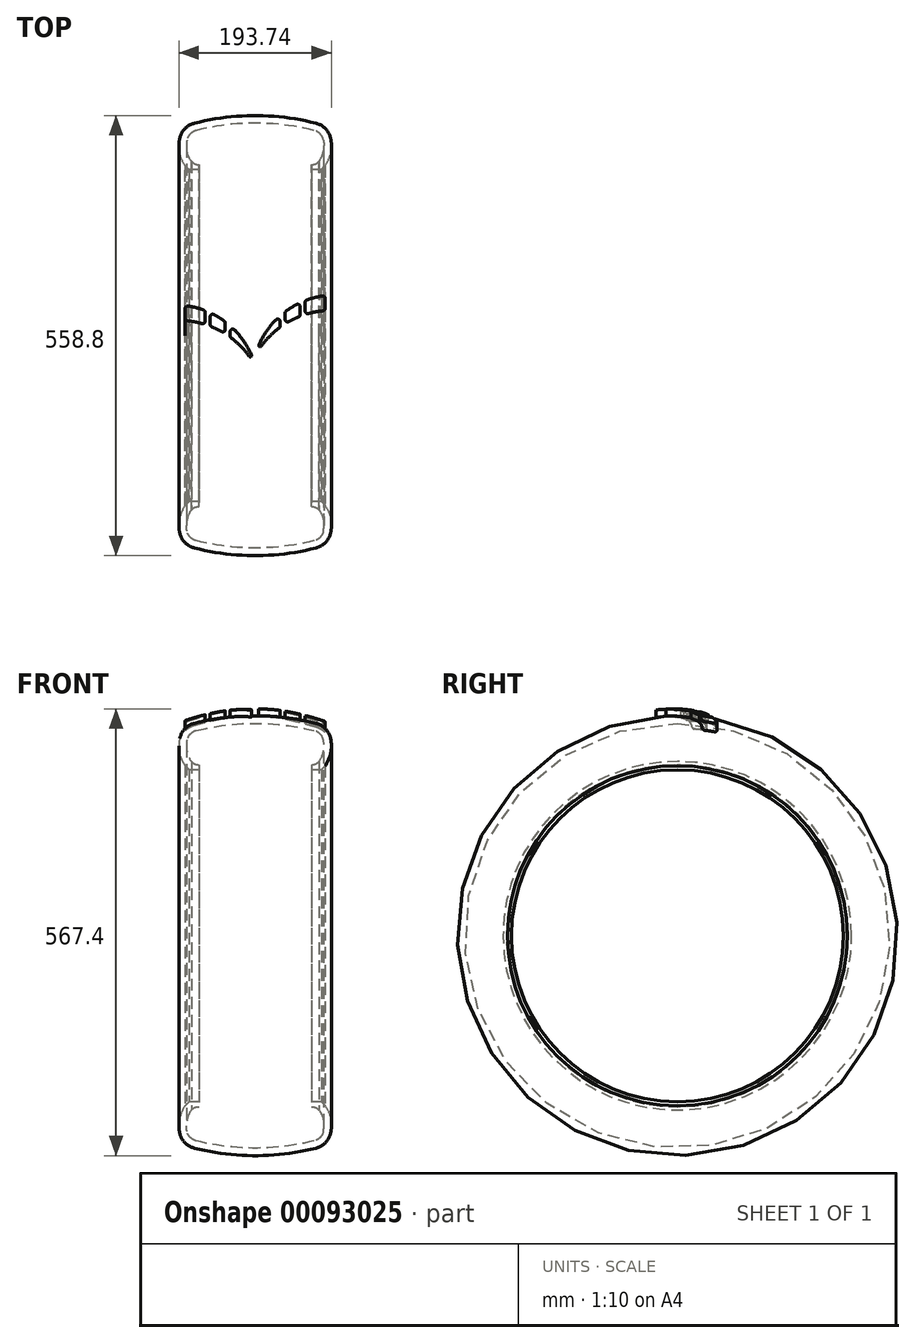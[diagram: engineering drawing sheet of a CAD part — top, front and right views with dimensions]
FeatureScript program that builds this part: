
annotation { "Feature Type Name" : "Feature", "Feature Type Description" : "" }
export const myFeature = defineFeature(function(context is Context, id is Id, definition is map)
    precondition{}
    {
        {
            var Q0;
            Q0=qCreatedBy(makeId("Front.planeOp"),FACE);
            var sketch = newSketch(context, id + "F0", { "sketchPlane" : qUnion([Q0])});
            skLineSegment(sketch, "E0", {"start": v(0, 0) * mm, "end": v(0, -279.4) * mm, "construction": true});
            skLineSegment(sketch, "E1", {"start": v(71.37, -210.82) * mm, "end": v(84.07, -210.82) * mm});
            skLineSegment(sketch, "E2", {"start": v(84.07, -210.82) * mm, "end": v(88.9, -215.9) * mm});
            skLineSegment(sketch, "E3.MirrorCS", {"start": v(-71.37, -210.82) * mm, "end": v(-84.07, -210.82) * mm});
            skLineSegment(sketch, "E4.MirrorCS", {"start": v(-84.07, -210.82) * mm, "end": v(-88.9, -215.9) * mm});
            skArc(sketch, "E5", {"start": v(95.92, -250.46) * mm, "mid": v(95.98, -232.45) * mm, "end": v(88.9, -215.9) * mm});
            skArc(sketch, "E6", {"start": v(0, -279.4) * mm, "mid": v(38.91, -277) * mm, "end": v(77.24, -269.86) * mm});
            skPoint(sketch, "E7.visualSharp", {"position": v(88.9, -266.7) * mm});
            skArc(sketch, "E7.filletArc", {"start": v(77.24, -269.86) * mm, "mid": v(89.36, -262.84) * mm, "end": v(95.92, -250.46) * mm});
            skArc(sketch, "E8.MirrorCS", {"start": v(0, -279.4) * mm, "mid": v(-38.91, -277) * mm, "end": v(-77.24, -269.86) * mm});
            skArc(sketch, "E9.MirrorCS", {"start": v(-77.24, -269.86) * mm, "mid": v(-89.36, -262.84) * mm, "end": v(-95.92, -250.46) * mm});
            skArc(sketch, "E10.MirrorCS", {"start": v(-95.92, -250.46) * mm, "mid": v(-95.98, -232.45) * mm, "end": v(-88.9, -215.9) * mm});
            skLineSegment(sketch, "E11", {"start": v(71.37, -210.82) * mm, "end": v(71.37, -217.17) * mm});
            skArc(sketch, "E12.0", {"start": v(86.6, -248.5) * mm, "mid": v(86.65, -234.35) * mm, "end": v(81.08, -221.34) * mm});
            skArc(sketch, "E13.0", {"start": v(0, -269.88) * mm, "mid": v(37.75, -267.55) * mm, "end": v(74.93, -260.62) * mm});
            skArc(sketch, "E14", {"start": v(74.93, -260.62) * mm, "mid": v(82.5, -256.23) * mm, "end": v(86.6, -248.5) * mm});
            skArc(sketch, "E15", {"start": v(81.08, -221.34) * mm, "mid": v(76.68, -218.2) * mm, "end": v(71.37, -217.17) * mm});
            skArc(sketch, "E16.MirrorCS", {"start": v(0, -269.88) * mm, "mid": v(-37.75, -267.55) * mm, "end": v(-74.93, -260.62) * mm});
            skArc(sketch, "E17.MirrorCS", {"start": v(-74.93, -260.62) * mm, "mid": v(-82.5, -256.23) * mm, "end": v(-86.6, -248.5) * mm});
            skArc(sketch, "E18.MirrorCS", {"start": v(-86.6, -248.5) * mm, "mid": v(-86.65, -234.35) * mm, "end": v(-81.08, -221.34) * mm});
            skArc(sketch, "E19.MirrorCS", {"start": v(-81.08, -221.34) * mm, "mid": v(-76.68, -218.2) * mm, "end": v(-71.37, -217.17) * mm});
            skLineSegment(sketch, "E20.MirrorCS", {"start": v(-71.37, -210.82) * mm, "end": v(-71.37, -217.17) * mm});
            skLineSegment(sketch, "E21", {"start": v(-88.9, 0) * mm, "end": v(88.9, 0) * mm, "construction": true});
            skSolve(sketch);
        }
        {
            var Q0;
            Q0 = qSketchRegion(id + "F0", true);
            var Q1;
            Q1=sQuery(id+"F0.wireOp",EDGE,"E21");
            revolve(context, id + "F1", {"entities" : qUnion([Q0]), "axis" : qUnion([Q1]), "revolveType" : RevolveType.FULL});
        }
        {
            var Q0;
            Q0=qCreatedBy(makeId("Top.planeOp"),FACE);
            cPlane(context, id + "F2", {"entities" : qUnion([Q0]), "cplaneType" : CPlaneType.OFFSET, "offset" : 304.8 * mm, "width" : 152.4 * mm, "height" : 152.4 * mm});
        }
        {
            var Q0;
            Q0=qCreatedBy(id+"F2.planeOp",FACE);
            var sketch = newSketch(context, id + "F3", { "sketchPlane" : qUnion([Q0])});
            skLineSegment(sketch, "E22", {"start": v(-88.9, 0) * mm, "end": v(88.9, 0) * mm, "construction": true});
            skLineSegment(sketch, "E23", {"start": v(0, 38.1) * mm, "end": v(0, -38.1) * mm, "construction": true});
            skArc(sketch, "E24", {"start": v(-4.72, -24.81) * mm, "mid": v(-14.03, -7.76) * mm, "end": v(-26.31, 7.29) * mm});
            skLineSegment(sketch, "E25", {"start": v(-88.9, 34.45) * mm, "end": v(-88.9, 21.95) * mm});
            skArc(sketch, "E26", {"start": v(-7.46, -26.38) * mm, "mid": v(-18.1, -13.82) * mm, "end": v(-30.48, -2.97) * mm});
            skLineSegment(sketch, "E27", {"start": v(-63.5, 29.55) * mm, "end": v(-63.5, 18.36) * mm});
            skLineSegment(sketch, "E28", {"start": v(-57.15, 23.94) * mm, "end": v(-57.15, 14) * mm});
            skLineSegment(sketch, "E29", {"start": v(-38.1, 16.03) * mm, "end": v(-38.1, 7.86) * mm});
            skLineSegment(sketch, "E30", {"start": v(-31.75, 5.06) * mm, "end": v(-31.75, -0.43) * mm});
            skArc(sketch, "E31.trimOffspring", {"start": v(-65.6, 32.53) * mm, "mid": v(-75.3, 35.54) * mm, "end": v(-85.23, 37.6) * mm});
            skArc(sketch, "E32.trimOffspring", {"start": v(-67.53, 15.3) * mm, "mid": v(-76.71, 17.44) * mm, "end": v(-86.05, 18.8) * mm});
            skArc(sketch, "E33.trimOffspring", {"start": v(-42.83, 5.1) * mm, "mid": v(-48.91, 8.27) * mm, "end": v(-55.18, 11.07) * mm});
            skArc(sketch, "E34.trimOffspring", {"start": v(-39.4, 18.6) * mm, "mid": v(-45.8, 22.91) * mm, "end": v(-52.5, 26.75) * mm});
            skPoint(sketch, "E35.visualSharp", {"position": v(-88.9, 38.1) * mm});
            skArc(sketch, "E35.filletArc", {"start": v(-85.23, 37.6) * mm, "mid": v(-87.79, 36.87) * mm, "end": v(-88.9, 34.45) * mm});
            skPoint(sketch, "E36.visualSharp", {"position": v(-88.9, 19.05) * mm});
            skArc(sketch, "E36.filletArc", {"start": v(-88.9, 21.95) * mm, "mid": v(-88.08, 19.83) * mm, "end": v(-86.05, 18.8) * mm});
            skPoint(sketch, "E37.visualSharp", {"position": v(-63.5, 14.1) * mm});
            skArc(sketch, "E37.filletArc", {"start": v(-67.53, 15.3) * mm, "mid": v(-64.75, 15.83) * mm, "end": v(-63.5, 18.36) * mm});
            skPoint(sketch, "E38.visualSharp", {"position": v(-63.5, 31.75) * mm});
            skArc(sketch, "E38.filletArc", {"start": v(-63.5, 29.55) * mm, "mid": v(-64.08, 31.37) * mm, "end": v(-65.6, 32.53) * mm});
            skPoint(sketch, "E39.visualSharp", {"position": v(-57.15, 29.05) * mm});
            skArc(sketch, "E39.filletArc", {"start": v(-52.5, 26.75) * mm, "mid": v(-55.62, 26.66) * mm, "end": v(-57.15, 23.94) * mm});
            skPoint(sketch, "E40.visualSharp", {"position": v(-57.15, 11.86) * mm});
            skArc(sketch, "E40.filletArc", {"start": v(-57.15, 14) * mm, "mid": v(-56.61, 12.24) * mm, "end": v(-55.18, 11.07) * mm});
            skPoint(sketch, "E41.visualSharp", {"position": v(-38.1, 2.28) * mm});
            skArc(sketch, "E41.filletArc", {"start": v(-42.83, 5.1) * mm, "mid": v(-39.67, 5.12) * mm, "end": v(-38.1, 7.86) * mm});
            skPoint(sketch, "E42.visualSharp", {"position": v(-38.1, 17.63) * mm});
            skArc(sketch, "E42.filletArc", {"start": v(-38.1, 16.03) * mm, "mid": v(-38.44, 17.47) * mm, "end": v(-39.4, 18.6) * mm});
            skPoint(sketch, "E43.visualSharp", {"position": v(-31.75, 12.45) * mm});
            skArc(sketch, "E43.filletArc", {"start": v(-26.31, 7.29) * mm, "mid": v(-29.78, 8) * mm, "end": v(-31.75, 5.06) * mm});
            skPoint(sketch, "E44.visualSharp", {"position": v(-31.75, -2.03) * mm});
            skArc(sketch, "E44.filletArc", {"start": v(-31.75, -0.43) * mm, "mid": v(-31.42, -1.85) * mm, "end": v(-30.48, -2.97) * mm});
            skPoint(sketch, "E45.visualSharp", {"position": v(0, -38.1) * mm});
            skArc(sketch, "E45.filletArc", {"start": v(-7.46, -26.38) * mm, "mid": v(-5.39, -26.82) * mm, "end": v(-4.72, -24.81) * mm});
            skPoint(sketch, "E46", {"position": v(0, -25.4) * mm});
            skLineSegment(sketch, "E47", {"start": v(88.9, 34.65) * mm, "end": v(88.9, 47.15) * mm});
            skArc(sketch, "E48", {"start": v(85.23, 50.3) * mm, "mid": v(75.3, 48.24) * mm, "end": v(65.6, 45.23) * mm});
            skArc(sketch, "E49", {"start": v(86.05, 31.5) * mm, "mid": v(76.71, 30.14) * mm, "end": v(67.53, 28) * mm});
            skLineSegment(sketch, "E50", {"start": v(63.5, 42.25) * mm, "end": v(63.5, 31.06) * mm});
            skLineSegment(sketch, "E51", {"start": v(57.15, 36.64) * mm, "end": v(57.15, 26.7) * mm});
            skLineSegment(sketch, "E52", {"start": v(38.1, 28.73) * mm, "end": v(38.1, 20.56) * mm});
            skLineSegment(sketch, "E53", {"start": v(31.75, 17.76) * mm, "end": v(31.75, 12.27) * mm});
            skArc(sketch, "E54.trimOffspring", {"start": v(26.31, 19.99) * mm, "mid": v(14.03, 4.94) * mm, "end": v(4.72, -12.11) * mm});
            skArc(sketch, "E55.trimOffspring", {"start": v(30.48, 9.73) * mm, "mid": v(18.1, -1.12) * mm, "end": v(7.46, -13.68) * mm});
            skArc(sketch, "E56.trimOffspring", {"start": v(55.18, 23.77) * mm, "mid": v(48.91, 20.97) * mm, "end": v(42.83, 17.8) * mm});
            skArc(sketch, "E57.trimOffspring", {"start": v(52.5, 39.45) * mm, "mid": v(45.8, 35.61) * mm, "end": v(39.4, 31.3) * mm});
            skPoint(sketch, "E58.visualSharp", {"position": v(88.9, 50.8) * mm});
            skArc(sketch, "E58.filletArc", {"start": v(88.9, 47.15) * mm, "mid": v(87.79, 49.57) * mm, "end": v(85.23, 50.3) * mm});
            skPoint(sketch, "E59.visualSharp", {"position": v(88.9, 31.75) * mm});
            skArc(sketch, "E59.filletArc", {"start": v(86.05, 31.5) * mm, "mid": v(88.08, 32.53) * mm, "end": v(88.9, 34.65) * mm});
            skPoint(sketch, "E60.visualSharp", {"position": v(63.5, 26.8) * mm});
            skArc(sketch, "E60.filletArc", {"start": v(63.5, 31.06) * mm, "mid": v(64.75, 28.53) * mm, "end": v(67.53, 28) * mm});
            skPoint(sketch, "E61.visualSharp", {"position": v(63.5, 44.45) * mm});
            skArc(sketch, "E61.filletArc", {"start": v(65.6, 45.23) * mm, "mid": v(64.08, 44.07) * mm, "end": v(63.5, 42.25) * mm});
            skPoint(sketch, "E62.visualSharp", {"position": v(57.15, 41.75) * mm});
            skArc(sketch, "E62.filletArc", {"start": v(57.15, 36.64) * mm, "mid": v(55.62, 39.36) * mm, "end": v(52.5, 39.45) * mm});
            skPoint(sketch, "E63.visualSharp", {"position": v(57.15, 24.56) * mm});
            skArc(sketch, "E63.filletArc", {"start": v(55.18, 23.77) * mm, "mid": v(56.61, 24.94) * mm, "end": v(57.15, 26.7) * mm});
            skPoint(sketch, "E64.visualSharp", {"position": v(38.1, 14.98) * mm});
            skArc(sketch, "E64.filletArc", {"start": v(38.1, 20.56) * mm, "mid": v(39.67, 17.82) * mm, "end": v(42.83, 17.8) * mm});
            skPoint(sketch, "E65.visualSharp", {"position": v(38.1, 30.33) * mm});
            skArc(sketch, "E65.filletArc", {"start": v(39.4, 31.3) * mm, "mid": v(38.44, 30.17) * mm, "end": v(38.1, 28.73) * mm});
            skPoint(sketch, "E66.visualSharp", {"position": v(31.75, 25.15) * mm});
            skArc(sketch, "E66.filletArc", {"start": v(31.75, 17.76) * mm, "mid": v(29.78, 20.7) * mm, "end": v(26.31, 19.99) * mm});
            skPoint(sketch, "E67.visualSharp", {"position": v(31.75, 10.67) * mm});
            skArc(sketch, "E67.filletArc", {"start": v(30.48, 9.73) * mm, "mid": v(31.42, 10.85) * mm, "end": v(31.75, 12.27) * mm});
            skArc(sketch, "E68.filletArc", {"start": v(4.72, -12.11) * mm, "mid": v(5.39, -14.12) * mm, "end": v(7.46, -13.68) * mm});
            skSolve(sketch);
        }
        {
            var Q0;
            Q0=qCreatedBy(makeId("Front.planeOp"),FACE);
            var sketch = newSketch(context, id + "F4", { "sketchPlane" : qUnion([Q0])});
            skLineSegment(sketch, "E69", {"start": v(-92.07, 273.05) * mm, "end": v(92.07, 273.05) * mm, "construction": true});
            skLineSegment(sketch, "E70", {"start": v(0, 0) * mm, "end": v(0, 273.05) * mm, "construction": true});
            skArc(sketch, "E71", {"start": v(92.07, 273.05) * mm, "mid": v(0, 288.16) * mm, "end": v(-92.08, 273.05) * mm});
            skLineSegment(sketch, "E72", {"start": v(-92.07, 273.05) * mm, "end": v(-92.07, 311.15) * mm});
            skLineSegment(sketch, "E73", {"start": v(-92.08, 311.15) * mm, "end": v(92.08, 311.15) * mm});
            skLineSegment(sketch, "E74", {"start": v(92.07, 311.15) * mm, "end": v(92.07, 273.05) * mm});
            skSolve(sketch);
        }
        {
            var Q0;
            Q0 = qSketchRegion(id + "F3", true);
            extrude(context, id + "F5", {"entities" : qUnion([Q0]), "operationType" : NewBodyOperationType.ADD, "endBound" : BoundingType.UP_TO_NEXT, "oppositeDirection" : true, "depth" : 25.4 * mm});
        }
        {
            var Q0;
            Q0 = qSketchRegion(id + "F4", true);
            var Q1;
            Q1=sQuery(id+"F0.wireOp",EDGE,"E21");
            revolve(context, id + "F6", {"operationType" : NewBodyOperationType.REMOVE, "entities" : qUnion([Q0]), "axis" : qUnion([Q1]), "revolveType" : RevolveType.FULL, "oppositeDirection" : true});
        }
    });
